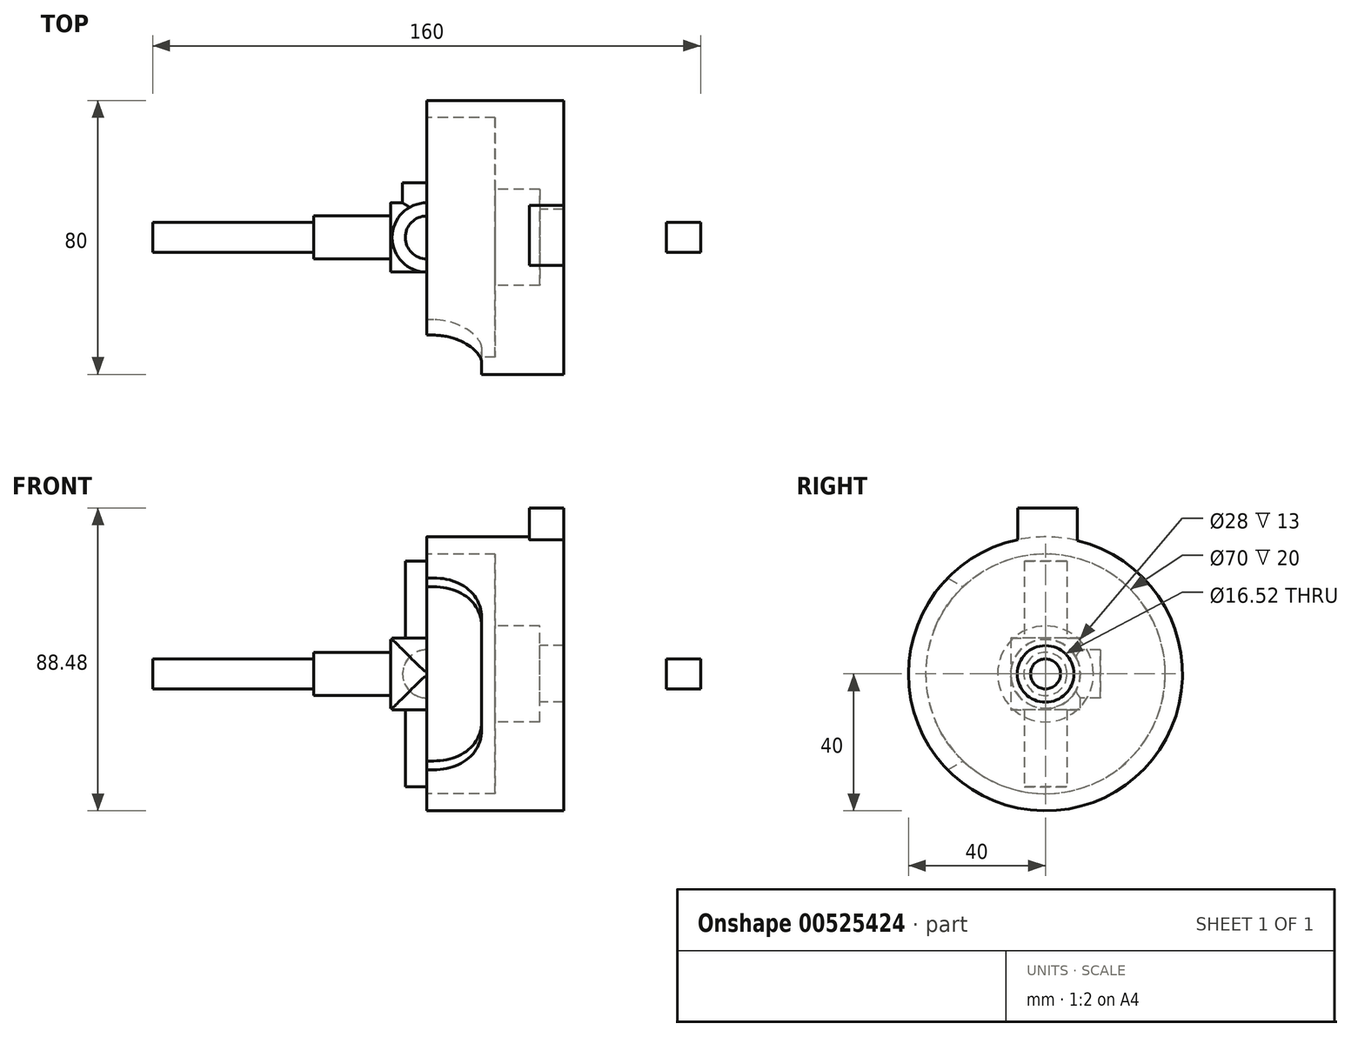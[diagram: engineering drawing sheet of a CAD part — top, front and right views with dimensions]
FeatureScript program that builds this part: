
annotation { "Feature Type Name" : "Feature", "Feature Type Description" : "" }
export const myFeature = defineFeature(function(context is Context, id is Id, definition is map)
    precondition{}
    {
        {
            var Q0;
            Q0=qCreatedBy(makeId("Top.planeOp"),FACE);
            var sketch = newSketch(context, id + "F0", { "sketchPlane" : qUnion([Q0])});
            skCircle(sketch, "E0", {"center": v(0, 0) * mm, "radius": 6.25 * mm});
            skSolve(sketch);
        }
        {
            var Q0;
            Q0 = qSketchRegion(id + "F0", true);
            extrude(context, id + "F1", {"entities" : qUnion([Q0]), "endBound" : BoundingType.SYMMETRIC, "depth" : 66 * mm, "offsetDistance" : 25 * mm});
        }
        {
            var Q0;
            Q0=qCreatedBy(makeId("Right.planeOp"),FACE);
            var sketch = newSketch(context, id + "F2", { "sketchPlane" : qUnion([Q0])});
            skCircle(sketch, "E1", {"center": v(0, 0) * mm, "radius": 6.3 * mm});
            skSolve(sketch);
        }
        {
            var Q0;
            Q0 = qSketchRegion(id + "F2", true);
            extrude(context, id + "F3", {"entities" : qUnion([Q0]), "operationType" : NewBodyOperationType.ADD, "endBound" : BoundingType.SYMMETRIC, "depth" : 66 * mm, "offsetDistance" : 25 * mm});
        }
        {
            var Q0;
            Q0=qCreatedBy(makeId("Top.planeOp"),FACE);
            var sketch = newSketch(context, id + "F4", { "sketchPlane" : qUnion([Q0])});
            skCircle(sketch, "E2", {"center": v(0, 0) * mm, "radius": 10.1 * mm});
            skSolve(sketch);
        }
        {
            var Q0;
            Q0 = qSketchRegion(id + "F4", true);
            extrude(context, id + "F5", {"entities" : qUnion([Q0]), "operationType" : NewBodyOperationType.ADD, "endBound" : BoundingType.SYMMETRIC, "depth" : 21 * mm, "offsetDistance" : 25 * mm});
        }
        {
            var Q0;
            Q0=qCreatedBy(makeId("Right.planeOp"),FACE);
            var sketch = newSketch(context, id + "F6", { "sketchPlane" : qUnion([Q0])});
            skCircle(sketch, "E3", {"center": v(0, 0) * mm, "radius": 10.13 * mm});
            skSolve(sketch);
        }
        {
            var Q0;
            Q0 = qSketchRegion(id + "F6", true);
            extrude(context, id + "F7", {"entities" : qUnion([Q0]), "operationType" : NewBodyOperationType.ADD, "endBound" : BoundingType.SYMMETRIC, "depth" : 21 * mm, "offsetDistance" : 25 * mm});
        }
        {
            var Q0;
            Q0=qCreatedBy(makeId("Front.planeOp"),FACE);
            var sketch = newSketch(context, id + "F8", { "sketchPlane" : qUnion([Q0])});
            skCircle(sketch, "E4", {"center": v(0, 0) * mm, "radius": 7.03 * mm});
            skSolve(sketch);
        }
        {
            var Q0;
            Q0 = qSketchRegion(id + "F8", true);
            extrude(context, id + "F9", {"entities" : qUnion([Q0]), "operationType" : NewBodyOperationType.ADD, "oppositeDirection" : true, "depth" : 16 * mm, "offsetDistance" : 25 * mm});
        }
        {
            var Q0;
            Q0=qCreatedBy(makeId("Right.planeOp"),FACE);
            var sketch = newSketch(context, id + "F10", { "sketchPlane" : qUnion([Q0])});
            skCircle(sketch, "E5", {"center": v(0, 0) * mm, "radius": 40 * mm});
            skCircle(sketch, "E6", {"center": v(0, 0) * mm, "radius": 35 * mm});
            skCircle(sketch, "E7", {"center": v(0, 0) * mm, "radius": 14 * mm});
            skSolve(sketch);
        }
        {
            var Q0;
            Q0=makeQuery(id+"F10.imprint","IMPRINT",FACE,{"disambiguationData":[TD([[makeQuery(id+"F10.imprint","IMPRINT",EDGE,{"derivedFrom":sQuery(id+"F10.wireOp",EDGE,"E5")}),1.0]])]});
            var Q1;
            Q1=makeQuery(id+"F10.imprint","IMPRINT",FACE,{"disambiguationData":[TD([[makeQuery(id+"F10.imprint","IMPRINT",EDGE,{"derivedFrom":sQuery(id+"F10.wireOp",EDGE,"E6")}),1.0]])]});
            var Q2;
            Q2=makeQuery(id+"F10.imprint","IMPRINT",FACE,{"disambiguationData":[TD([[makeQuery(id+"F10.imprint","IMPRINT",EDGE,{"derivedFrom":sQuery(id+"F10.wireOp",EDGE,"E7")}),1.0]])]});
            extrude(context, id + "F11", {"entities" : qUnion([Q0, Q1, Q2]), "depth" : 40 * mm, "offsetDistance" : 25 * mm});
        }
        {
            var Q0;
            Q0=makeQuery(id+"F10.imprint","IMPRINT",FACE,{"disambiguationData":[TD([[makeQuery(id+"F10.imprint","IMPRINT",EDGE,{"derivedFrom":sQuery(id+"F10.wireOp",EDGE,"E6")}),1.0]])]});
            extrude(context, id + "F12", {"entities" : qUnion([Q0]), "operationType" : NewBodyOperationType.REMOVE, "depth" : 20 * mm, "offsetDistance" : 25 * mm});
        }
        {
            var Q0;
            Q0=makeQuery(id+"F10.imprint","IMPRINT",FACE,{"disambiguationData":[TD([[makeQuery(id+"F10.imprint","IMPRINT",EDGE,{"derivedFrom":sQuery(id+"F10.wireOp",EDGE,"E7")}),1.0]])]});
            extrude(context, id + "F13", {"entities" : qUnion([Q0]), "operationType" : NewBodyOperationType.REMOVE, "depth" : 33 * mm, "offsetDistance" : 25 * mm});
        }
        {
            var Q0;
            Q0=qCreatedBy(makeId("Right.planeOp"),FACE);
            var sketch = newSketch(context, id + "F14", { "sketchPlane" : qUnion([Q0])});
            skLineSegment(sketch, "E8", {"start": v(0, 0) * mm, "end": v(-54.2, 0) * mm, "construction": true});
            skLineSegment(sketch, "E9", {"start": v(0, 0) * mm, "end": v(-32.72, 18.89) * mm, "construction": true});
            skLineSegment(sketch, "E10", {"start": v(-29.43, 28.54) * mm, "end": v(-7.96, 16.14) * mm});
            skArc(sketch, "E11", {"start": v(-29.43, 28.54) * mm, "mid": v(-41, 0) * mm, "end": v(-29.43, -28.54) * mm});
            skArc(sketch, "E12", {"start": v(-7.96, 16.14) * mm, "mid": v(-18, 0) * mm, "end": v(-7.96, -16.14) * mm});
            skLineSegment(sketch, "E13.MirrorCS", {"start": v(-29.43, -28.54) * mm, "end": v(-7.96, -16.14) * mm});
            skSolve(sketch);
        }
        {
            var Q0;
            Q0 = qSketchRegion(id + "F14", true);
            extrude(context, id + "F15", {"entities" : qUnion([Q0]), "operationType" : NewBodyOperationType.REMOVE, "depth" : 16 * mm, "offsetDistance" : 25 * mm});
        }
        {
            var Q0;
            Q0=makeQuery(id+"F15.boolean.opBoolean","COPY",EDGE,{"derivedFrom":makeQuery(id+"F15.opExtrude","CAP_EDGE",EDGE,{"disambiguationData":[OSD([sQuery(id+"F14.wireOp",EDGE,"E10")])],"isStart":false})});
            var Q1;
            Q1=makeQuery(id+"F15.boolean.opBoolean","COPY",EDGE,{"derivedFrom":makeQuery(id+"F15.opExtrude","CAP_EDGE",EDGE,{"disambiguationData":[OSD([sQuery(id+"F14.wireOp",EDGE,"E13.MirrorCS")])],"isStart":false})});
            fillet(context, id + "F16", {"entities" : qUnion([Q0, Q1]), "radius" : 14 * mm, "tangentPropagation" : true, "allowEdgeOverflow" : false});
        }
        {
            var Q0;
            Q0=makeQuery(id+"F11.opExtrude","CAP_FACE",FACE,{"disambiguationData":[OSD([sQuery(id+"F10.wireOp",EDGE,"E5")])],"isStart":false});
            var sketch = newSketch(context, id + "F17", { "sketchPlane" : qUnion([Q0])});
            skLineSegment(sketch, "E14.bottom", {"start": v(9.3, 48.48) * mm, "end": v(-8.13, 48.48) * mm});
            skLineSegment(sketch, "E14.top", {"start": v(9.3, 17.13) * mm, "end": v(-8.13, 17.13) * mm});
            skLineSegment(sketch, "E14.left", {"start": v(9.3, 48.48) * mm, "end": v(9.3, 17.13) * mm});
            skLineSegment(sketch, "E14.right", {"start": v(-8.13, 48.48) * mm, "end": v(-8.13, 17.13) * mm});
            skSolve(sketch);
        }
        {
            var Q0;
            Q0 = qSketchRegion(id + "F17", true);
            extrude(context, id + "F18", {"entities" : qUnion([Q0]), "operationType" : NewBodyOperationType.ADD, "oppositeDirection" : true, "depth" : 10 * mm, "offsetDistance" : 25 * mm});
        }
        {
            var Q0;
            Q0=qCreatedBy(makeId("Right.planeOp"),FACE);
            var sketch = newSketch(context, id + "F19", { "sketchPlane" : qUnion([Q0])});
            skCircle(sketch, "E15", {"center": v(0, 0) * mm, "radius": 4.38 * mm});
            skSolve(sketch);
        }
        {
            var Q0;
            Q0 = qSketchRegion(id + "F19", true);
            extrude(context, id + "F20", {"entities" : qUnion([Q0]), "operationType" : NewBodyOperationType.ADD, "endBound" : BoundingType.SYMMETRIC, "depth" : 160 * mm, "offsetDistance" : 25 * mm});
        }
        {
            var Q0;
            Q0=qCreatedBy(makeId("Right.planeOp"),FACE);
            var sketch = newSketch(context, id + "F21", { "sketchPlane" : qUnion([Q0])});
            skCircle(sketch, "E16", {"center": v(0, 0) * mm, "radius": 8.26 * mm});
            skSolve(sketch);
        }
        {
            var Q0;
            Q0 = qSketchRegion(id + "F21", true);
            extrude(context, id + "F22", {"entities" : qUnion([Q0]), "operationType" : NewBodyOperationType.REMOVE, "depth" : 70 * mm, "offsetDistance" : 25 * mm});
        }
    });
